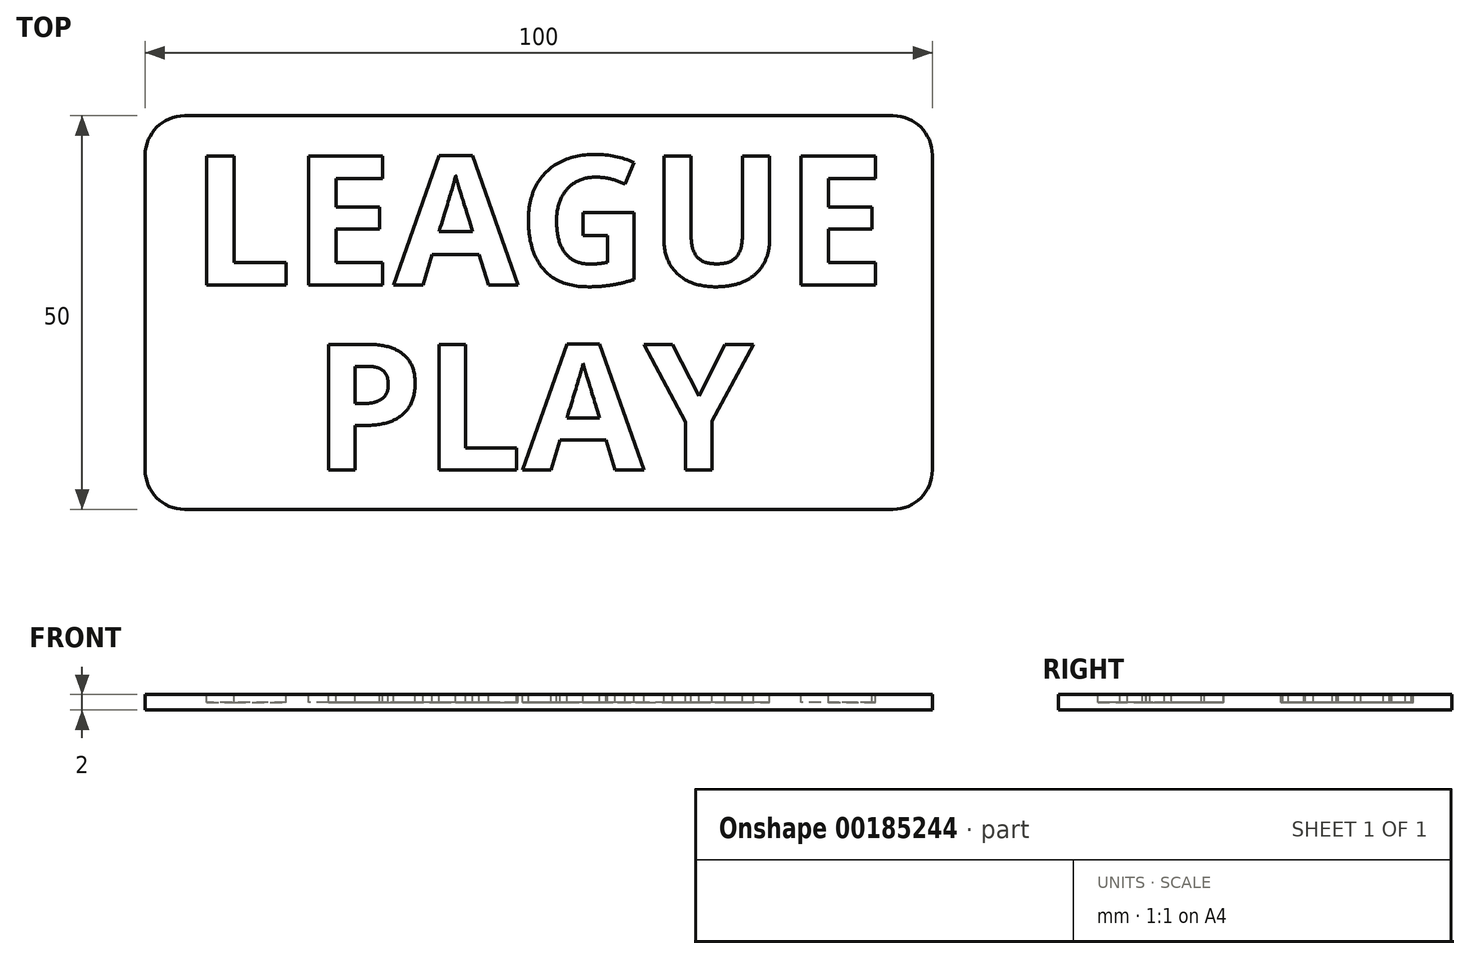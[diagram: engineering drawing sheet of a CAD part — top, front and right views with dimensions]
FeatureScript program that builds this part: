
annotation { "Feature Type Name" : "Feature", "Feature Type Description" : "" }
export const myFeature = defineFeature(function(context is Context, id is Id, definition is map)
    precondition{}
    {
        {
            var Q0;
            Q0=qCreatedBy(makeId("Top.planeOp"),FACE);
            var sketch = newSketch(context, id + "F0", { "sketchPlane" : qUnion([Q0])});
            skLineSegment(sketch, "E0.bottom", {"start": v(45, -25) * mm, "end": v(-45, -25) * mm});
            skLineSegment(sketch, "E0.top", {"start": v(45, 25) * mm, "end": v(-45, 25) * mm});
            skLineSegment(sketch, "E0.left", {"start": v(50, -20) * mm, "end": v(50, 20) * mm});
            skLineSegment(sketch, "E0.right", {"start": v(-50, -20) * mm, "end": v(-50, 20) * mm});
            skPoint(sketch, "E0.middle", {"position": v(0, 0) * mm});
            skPoint(sketch, "E1.visualSharp", {"position": v(-50, 25) * mm});
            skArc(sketch, "E1.filletArc", {"start": v(-45, 25) * mm, "mid": v(-48.54, 23.54) * mm, "end": v(-50, 20) * mm});
            skPoint(sketch, "E2.visualSharp", {"position": v(50, 25) * mm});
            skArc(sketch, "E2.filletArc", {"start": v(50, 20) * mm, "mid": v(48.54, 23.54) * mm, "end": v(45, 25) * mm});
            skPoint(sketch, "E3.visualSharp", {"position": v(50, -25) * mm});
            skArc(sketch, "E3.filletArc", {"start": v(45, -25) * mm, "mid": v(48.54, -23.54) * mm, "end": v(50, -20) * mm});
            skPoint(sketch, "E4.visualSharp", {"position": v(-50, -25) * mm});
            skArc(sketch, "E4.filletArc", {"start": v(-50, -20) * mm, "mid": v(-48.54, -23.54) * mm, "end": v(-45, -25) * mm});
            skSolve(sketch);
        }
        {
            var Q0;
            Q0 = qSketchRegion(id + "F0", true);
            extrude(context, id + "F1", {"entities" : qUnion([Q0]), "depth" : 2 * mm});
        }
        {
            var Q0;
            Q0=makeQuery(id+"F1.opExtrude","CAP_FACE",FACE,{"disambiguationData":[OSD([sQuery(id+"F0.wireOp",EDGE,"E0.bottom"),sQuery(id+"F0.wireOp",EDGE,"E0.top"),sQuery(id+"F0.wireOp",EDGE,"E0.left"),sQuery(id+"F0.wireOp",EDGE,"E0.right")])],"isStart":false});
            var sketch = newSketch(context, id + "F2", { "sketchPlane" : qUnion([Q0])});
            skText(sketch, "E5", { "text": "LEAGUE", "fontName": "OpenSans-Bold.ttf"});
            skText(sketch, "E6", { "text": "PLAY", "fontName": "OpenSans-Bold.ttf"});
            skLineSegment(sketch, "E7", {"start": v(0, 25) * mm, "end": v(0, 20) * mm, "construction": true});
            skLineSegment(sketch, "E8", {"start": v(0, -25) * mm, "end": v(0, -20) * mm, "construction": true});
            const initialGuessF2  = {"E5": [-0.04424, 0.0035, 1, 0, 0.0165], "E6": [-0.02873, -0.02, 1, 0, 0.01609]};
            skSetInitialGuess(sketch, initialGuessF2);
            skSolve(sketch);
        }
        {
            var Q0;
            Q0 = qSketchRegion(id + "F2", true);
            extrude(context, id + "F3", {"entities" : qUnion([Q0]), "operationType" : NewBodyOperationType.REMOVE, "oppositeDirection" : true, "depth" : 1 * mm});
        }
    });
